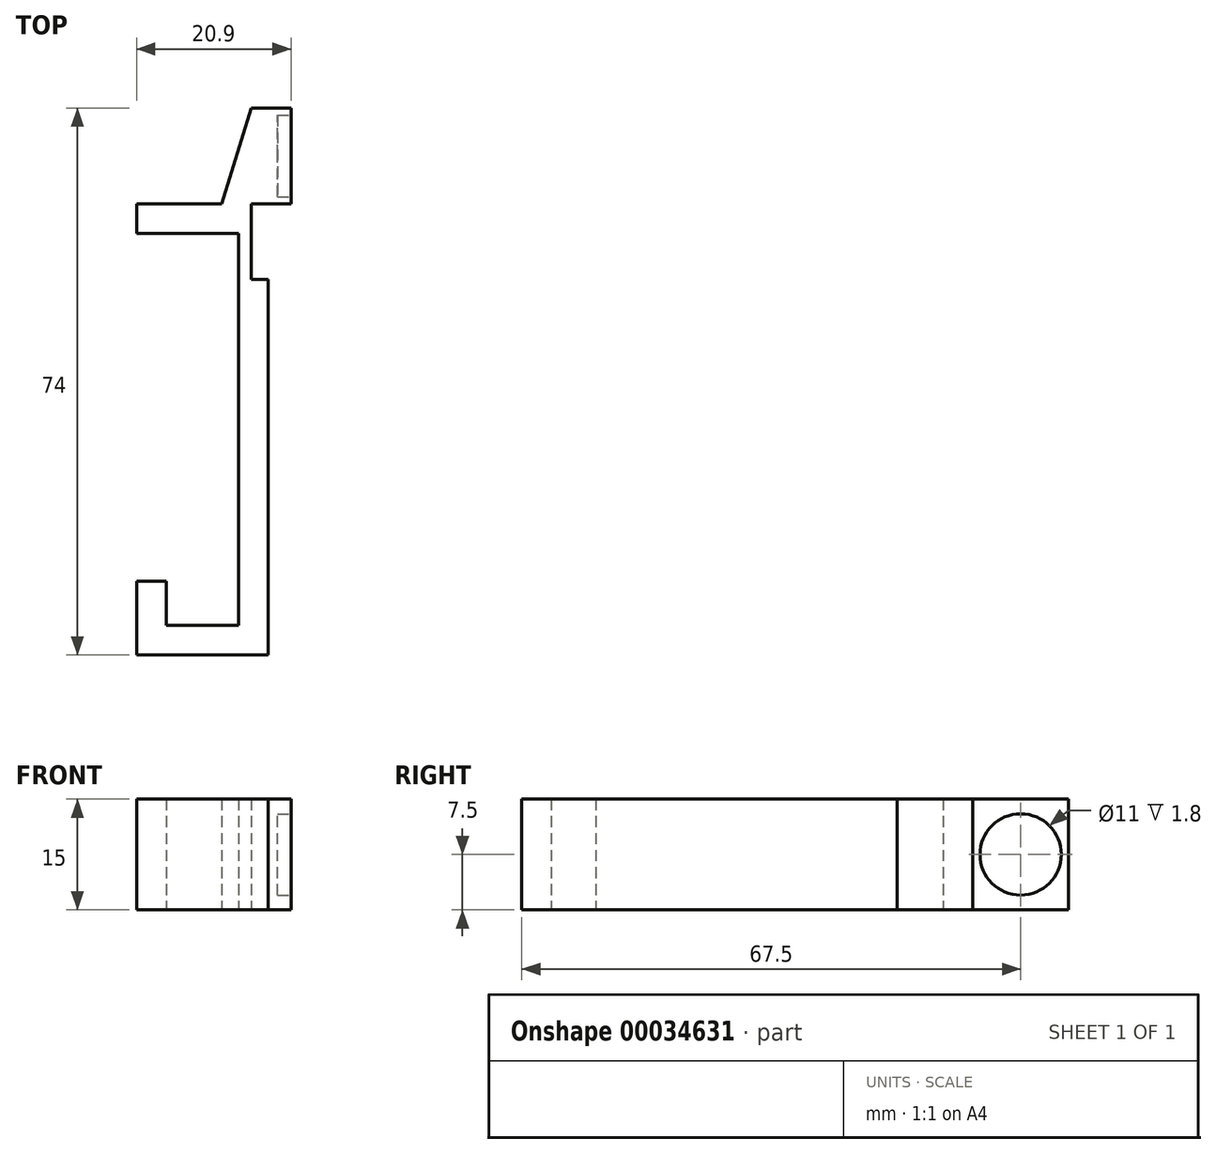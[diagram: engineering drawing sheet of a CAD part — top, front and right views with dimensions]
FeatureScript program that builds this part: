
annotation { "Feature Type Name" : "Feature", "Feature Type Description" : "" }
export const myFeature = defineFeature(function(context is Context, id is Id, definition is map)
    precondition{}
    {
        {
            var Q0;
            Q0=qCreatedBy(makeId("Top.planeOp"),FACE);
            var sketch = newSketch(context, id + "F0", { "sketchPlane" : qUnion([Q0])});
            skLineSegment(sketch, "E0.bottom", {"start": v(0, 0) * mm, "end": v(5.4, 0) * mm});
            skLineSegment(sketch, "E0.top", {"start": v(0, -13) * mm, "end": v(5.4, -13) * mm});
            skLineSegment(sketch, "E0.left", {"start": v(0, 0) * mm, "end": v(0, -13) * mm});
            skLineSegment(sketch, "E0.right", {"start": v(5.4, 0) * mm, "end": v(5.4, -13) * mm});
            skLineSegment(sketch, "E1.bottom", {"start": v(0, -13) * mm, "end": v(-4, -13) * mm});
            skLineSegment(sketch, "E1.top", {"start": v(0, -23.2) * mm, "end": v(-1.7, -23.2) * mm});
            skLineSegment(sketch, "E1.left", {"start": v(0, -13) * mm, "end": v(0, -23.2) * mm});
            skLineSegment(sketch, "E1.right", {"start": v(-4, -13) * mm, "end": v(-4, -17) * mm});
            skLineSegment(sketch, "E2.bottom", {"start": v(0, -23.2) * mm, "end": v(2.3, -23.2) * mm});
            skLineSegment(sketch, "E2.top", {"start": v(0, -70) * mm, "end": v(2.3, -70) * mm});
            skLineSegment(sketch, "E2.left", {"start": v(0, -23.2) * mm, "end": v(0, -70) * mm});
            skLineSegment(sketch, "E2.right", {"start": v(2.3, -23.2) * mm, "end": v(2.3, -70) * mm});
            skLineSegment(sketch, "E3.top", {"start": v(0, -70) * mm, "end": v(-1.7, -70) * mm});
            skLineSegment(sketch, "E4.bottom", {"start": v(2.3, -70) * mm, "end": v(-11.5, -70) * mm});
            skLineSegment(sketch, "E4.top", {"start": v(2.3, -74) * mm, "end": v(-11.5, -74) * mm});
            skLineSegment(sketch, "E4.left", {"start": v(2.3, -70) * mm, "end": v(2.3, -74) * mm});
            skLineSegment(sketch, "E4.right", {"start": v(-11.5, -70) * mm, "end": v(-11.5, -74) * mm});
            skLineSegment(sketch, "E5.bottom", {"start": v(-11.5, -74) * mm, "end": v(-15.5, -74) * mm});
            skLineSegment(sketch, "E5.top", {"start": v(-11.5, -64) * mm, "end": v(-15.5, -64) * mm});
            skLineSegment(sketch, "E5.left", {"start": v(-11.5, -74) * mm, "end": v(-11.5, -64) * mm});
            skLineSegment(sketch, "E5.right", {"start": v(-15.5, -74) * mm, "end": v(-15.5, -64) * mm});
            skLineSegment(sketch, "E6", {"start": v(-4, -13) * mm, "end": v(0, 0) * mm});
            skLineSegment(sketch, "E7", {"start": v(-1.7, -23.2) * mm, "end": v(-1.7, -70) * mm});
            skLineSegment(sketch, "E8.bottom", {"start": v(-4, -13) * mm, "end": v(-15.5, -13) * mm});
            skLineSegment(sketch, "E8.top", {"start": v(-4, -17) * mm, "end": v(-15.5, -17) * mm});
            skLineSegment(sketch, "E8.right", {"start": v(-15.5, -13) * mm, "end": v(-15.5, -17) * mm});
            skLineSegment(sketch, "E9.bottom", {"start": v(-15.5, -17) * mm, "end": v(-11.5, -17) * mm});
            skLineSegment(sketch, "E9.top", {"start": v(-15.5, -23) * mm, "end": v(-11.5, -23) * mm});
            skLineSegment(sketch, "E9.left", {"start": v(-15.5, -17) * mm, "end": v(-15.5, -23) * mm});
            skLineSegment(sketch, "E9.right", {"start": v(-11.5, -17) * mm, "end": v(-11.5, -23) * mm});
            skLineSegment(sketch, "E10", {"start": v(-1.7, -23.2) * mm, "end": v(-1.7, -13) * mm});
            skLineSegment(sketch, "E11", {"start": v(-4, -17) * mm, "end": v(-1.7, -17) * mm});
            skPoint(sketch, "E12", {"position": v(-5.7, -17) * mm});
            skPoint(sketch, "E13", {"position": v(-1.7, -19.92) * mm});
            skSolve(sketch);
        }
        {
            var Q0;
            Q0=makeQuery(id+"F0.imprint","IMPRINT",FACE,{"disambiguationData":[TD([[makeQuery(id+"F0.imprint","IMPRINT",EDGE,{"derivedFrom":sQuery(id+"F0.wireOp",EDGE,"E1.bottom")}),1.0]])]});
            var Q1;
            Q1=makeQuery(id+"F0.imprint","IMPRINT",FACE,{"disambiguationData":[TD([[makeQuery(id+"F0.imprint","IMPRINT",EDGE,{"derivedFrom":sQuery(id+"F0.wireOp",EDGE,"E0.bottom")}),-1.0]])]});
            var Q2;
            Q2=makeQuery(id+"F0.imprint","IMPRINT",FACE,{"disambiguationData":[TD([[makeQuery(id+"F0.imprint","IMPRINT",EDGE,{"derivedFrom":sQuery(id+"F0.wireOp",EDGE,"bd5864b2-4246-4288-8592-2cc1284bbe6f.bottom")}),-1.0]])]});
            var Q3;
            Q3=makeQuery(id+"F0.imprint","IMPRINT",FACE,{"disambiguationData":[TD([[makeQuery(id+"F0.imprint","IMPRINT",EDGE,{"derivedFrom":sQuery(id+"F0.wireOp",EDGE,"c464678c-0b4d-4f9e-8c93-3109acf3fdbd.bottom")}),1.0]])]});
            var Q4;
            {var subQ2=sQuery(id+"F0.wireOp",EDGE,"E1.top");Q4=makeQuery(id+"F0.imprint","IMPRINT",FACE,{"disambiguationData":[TD([[makeQuery(id+"F0.imprint","IMPRINT",EDGE,{"derivedFrom":subQ2}),1.0]])]});}
            var Q5;
            {var subQ3=sQuery(id+"F0.wireOp",EDGE,"E5.bottom");Q5=makeQuery(id+"F0.imprint","IMPRINT",FACE,{"disambiguationData":[TD([[makeQuery(id+"F0.imprint","IMPRINT",EDGE,{"derivedFrom":subQ3}),-1.0]])]});}
            var Q6;
            Q6=makeQuery(id+"F0.imprint","IMPRINT",FACE,{"disambiguationData":[TD([[makeQuery(id+"F0.imprint","IMPRINT",EDGE,{"derivedFrom":sQuery(id+"F0.wireOp",EDGE,"E2.bottom")}),-1.0]])]});
            var Q7;
            {var subQ1=sQuery(id+"F0.wireOp",EDGE,"E4.top");Q7=makeQuery(id+"F0.imprint","IMPRINT",FACE,{"disambiguationData":[TD([[makeQuery(id+"F0.imprint","IMPRINT",EDGE,{"derivedFrom":subQ1}),-1.0]])]});}
            var Q8;
            {var subQ5=sQuery(id+"F0.wireOp",EDGE,"E1.top");Q8=makeQuery(id+"F0.imprint","IMPRINT",FACE,{"disambiguationData":[TD([[makeQuery(id+"F0.imprint","IMPRINT",EDGE,{"derivedFrom":subQ5}),1.0]])]});}
            var Q9;
            Q9=makeQuery(id+"F0.imprint","IMPRINT",FACE,{"disambiguationData":[TD([[makeQuery(id+"F0.imprint","IMPRINT",EDGE,{"derivedFrom":sQuery(id+"F0.wireOp",EDGE,"E0.left")}),-1.0]])]});
            var Q10;
            Q10=makeQuery(id+"F0.imprint","IMPRINT",FACE,{"disambiguationData":[TD([[makeQuery(id+"F0.imprint","IMPRINT",EDGE,{"derivedFrom":sQuery(id+"F0.wireOp",EDGE,"e5485833-f8b7-4b19-b778-66beabb379ba.bottom")}),-1.0]])]});
            var Q11;
            Q11=makeQuery(id+"F0.imprint","IMPRINT",FACE,{"disambiguationData":[TD([[makeQuery(id+"F0.imprint","IMPRINT",EDGE,{"derivedFrom":sQuery(id+"F0.wireOp",EDGE,"5c71f5a1-6308-4ddc-b6fd-d370f590129d.top")}),1.0]])]});
            var Q12;
            Q12=makeQuery(id+"F0.imprint","IMPRINT",FACE,{"disambiguationData":[TD([[makeQuery(id+"F0.imprint","IMPRINT",EDGE,{"derivedFrom":sQuery(id+"F0.wireOp",EDGE,"4d46738f-46d7-4931-af52-41e0a387aeff.top")}),1.0]])]});
            var Q13;
            Q13=makeQuery(id+"F0.imprint","IMPRINT",FACE,{"disambiguationData":[TD([[makeQuery(id+"F0.imprint","IMPRINT",EDGE,{"derivedFrom":sQuery(id+"F0.wireOp",EDGE,"E8.bottom")}),1.0]])]});
            var Q14;
            Q14=makeQuery(id+"F0.imprint","IMPRINT",FACE,{"disambiguationData":[TD([[makeQuery(id+"F0.imprint","IMPRINT",EDGE,{"derivedFrom":sQuery(id+"F0.wireOp",EDGE,"E9.bottom")}),-1.0]])]});
            var Q15;
            {var subQ6=sQuery(id+"F0.wireOp",EDGE,"E1.left");Q15=makeQuery(id+"F0.imprint","IMPRINT",FACE,{"disambiguationData":[TD([[makeQuery(id+"F0.imprint","IMPRINT",EDGE,{"derivedFrom":subQ6}),-1.0]])]});}
            var Q16;
            {var subQ1=sQuery(id+"F0.wireOp",EDGE,"E11");Q16=makeQuery(id+"F0.imprint","IMPRINT",FACE,{"disambiguationData":[TD([[makeQuery(id+"F0.imprint","IMPRINT",EDGE,{"derivedFrom":subQ1}),-1.0]])]});}
            extrude(context, id + "F1", {"entities" : qUnion([Q0, Q1, Q2, Q3, Q4, Q5, Q6, Q7, Q8, Q9, Q10, Q11, Q12, Q13, Q14, Q15, Q16]), "depth" : 15 * mm});
        }
        {
            var Q0;
            Q0=makeQuery(id+"F1.opExtrude","SWEPT_FACE",FACE,{"disambiguationData":[OSD([sQuery(id+"F0.wireOp",EDGE,"E0.right")])]});
            var sketch = newSketch(context, id + "F2", { "sketchPlane" : qUnion([Q0])});
            skCircle(sketch, "E14", {"center": v(-6.5, 7.5) * mm, "radius": 5.5 * mm});
            skSolve(sketch);
        }
        {
            var Q0;
            Q0=makeQuery(id+"F2.imprint","IMPRINT",FACE,{"disambiguationData":[TD([[makeQuery(id+"F2.imprint","IMPRINT",EDGE,{"derivedFrom":sQuery(id+"F2.wireOp",EDGE,"E14")}),1.0]])]});
            var Q1;
            Q1=makeQuery(id+"F2.imprint","IMPRINT",FACE,{"disambiguationData":[TD([[makeQuery(id+"F2.imprint","IMPRINT",EDGE,{"derivedFrom":sQuery(id+"F2.wireOp",EDGE,"E14")}),1.0]])]});
            extrude(context, id + "F3", {"entities" : qUnion([Q0, Q1]), "operationType" : NewBodyOperationType.REMOVE, "oppositeDirection" : true, "depth" : 1.8 * mm});
        }
    });
